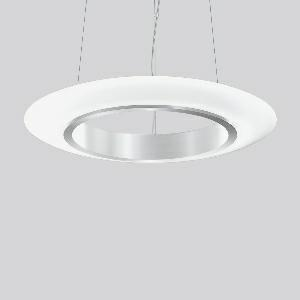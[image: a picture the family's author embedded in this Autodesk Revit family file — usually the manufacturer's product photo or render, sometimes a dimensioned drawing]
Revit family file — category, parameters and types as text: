
# Revit family: ring_of_fire_p_312546_004_76_1bfb
name_source: partatom
category: Lighting Fixtures
units: mm (PartAtom-declared; Revit-internal decimal feet)

## family parameters
Cut with Voids When Loaded = No
Host = Face
Light Source = No
Part Type = Normal
Room Calculation Point = No
Round Connector Dimension = Use Diameter
Shared = No

## types (1)
- RING OF FIRE P (1 x LED Modul 830, 5550 lm, 3000)
    Apparent Load = 71 VA
    CIE Flux Codes = 43 72 90 52 100
    Color Rendering = 80
    Color Temperature = 3000
    Default Elevation = 1800 mm
    Description = Series: RING OF FIRE
A uniquely shaped pendant luminaire with elliptical glass. Supporting ring made of anodised aluminium. Canopy aluminium anodised. Opal glass: mouth-blown, satin finish. Suitable for pendant. 3-point steel cable suspension, steplessly adjustable. Special lengths available on request. 
Colour: anodised aluminium
Diameter: 690 mm
Height: 81 mm
Suspension length: 500-1200 mm
Lamp: LED
Socket: without socket
Colour temperature: 3000K
Colour rendering index (CRI): 80
System power: 71 W
Rated luminous flux: 5550 lm
Luminous efficiency: 78 lm/W
Control gear: Converter, dimmable, DALI
Protection class: I
Type of protection: IP 20
    Height = 81 mm
    Lamp = 1 x LED Modul 830
    Lamp Light Flux = 5550 lm
    Lamp count = 1
    Length = 690 mm
    Lifetime = 50000 h
    Luminous efficacy = 78 lm/W
    Manufacturer = RZB
    ModVariant = No
    Model = 312546.004.76
    Mounting Place = Ceiling
    Mounting Type = Pendant
    Number of Poles = 1
    OnlyDefault = Yes
    Power Factor = 1
    Product Name = RING OF FIRE P
    Product group = Pendant luminaires
    ProductGroupID = 902
    Protection Class = Protection class I
    Protection Degree = IP 20
    RLX_Detail_Level = 1
    RLX_Emergency_Light_Flux = 0 lm
    RLX_Emergency_Type = 0
    RLX_Emergency_Type_DB = No
    RlxData = <blob elided: 30173 chars, md5=6f42e959>
    Socket = socket
    Standby Power = 0 W
    System Light Flux = 5550 lm
    System Power = 71 W
    Type Comments = Product without accessories
    Type Image = 311570.004.jpg
    URL = http://relux.com
    VarID = ---
    Voltage = 230 V
    Voltage Range = 220-240 V
    Weight = 0.00 kg
    Width = 0 mm  [stored 0 ft]

note: [stored X ft] marks values corroborated as IEEE doubles in the binary element streams (Revit-internal decimal feet)

## geometry (parser evidence)
native form markers: Blend x4, Sweep x12
no freeform markers — native parametric forms only
